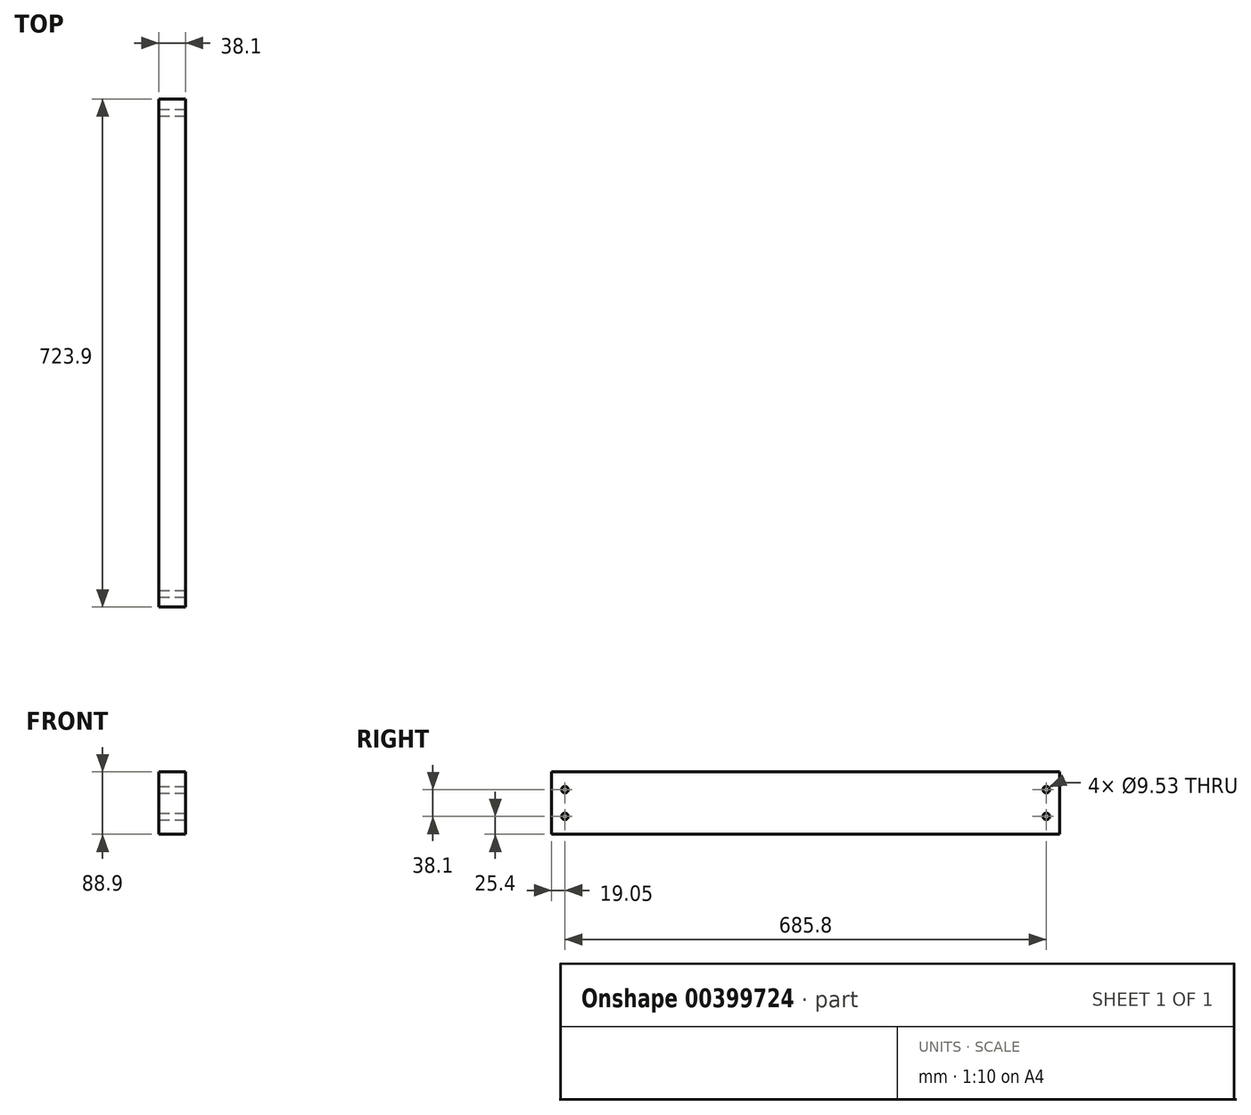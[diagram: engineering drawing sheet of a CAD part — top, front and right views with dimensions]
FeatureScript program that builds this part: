
annotation { "Feature Type Name" : "Feature", "Feature Type Description" : "" }
export const myFeature = defineFeature(function(context is Context, id is Id, definition is map)
    precondition{}
    {
        {
            var Q0;
            Q0=qCreatedBy(makeId("Front.planeOp"),FACE);
            var sketch = newSketch(context, id + "F0", { "sketchPlane" : qUnion([Q0])});
            skLineSegment(sketch, "E0.bottom", {"start": v(-19.05, 44.45) * mm, "end": v(19.05, 44.45) * mm});
            skLineSegment(sketch, "E0.top", {"start": v(-19.05, -44.45) * mm, "end": v(19.05, -44.45) * mm});
            skLineSegment(sketch, "E0.left", {"start": v(-19.05, 44.45) * mm, "end": v(-19.05, -44.45) * mm});
            skLineSegment(sketch, "E0.right", {"start": v(19.05, 44.45) * mm, "end": v(19.05, -44.45) * mm});
            skSolve(sketch);
        }
        {
            var Q0;
            Q0 = qSketchRegion(id + "F0", true);
            extrude(context, id + "F1", {"entities" : qUnion([Q0]), "endBound" : BoundingType.SYMMETRIC, "depth" : 723.9 * mm});
        }
        {
            var Q0;
            Q0=makeQuery(id+"F1.opExtrude","SWEPT_FACE",FACE,{"disambiguationData":[OSD([sQuery(id+"F0.wireOp",EDGE,"E0.right")])]});
            var sketch = newSketch(context, id + "F2", { "sketchPlane" : qUnion([Q0])});
            skCircle(sketch, "E1", {"center": v(-342.9, 19.05) * mm, "radius": 4.76 * mm});
            skCircle(sketch, "E2", {"center": v(-342.9, -19.05) * mm, "radius": 4.76 * mm});
            skCircle(sketch, "E3", {"center": v(342.9, 19.05) * mm, "radius": 4.76 * mm});
            skCircle(sketch, "E4", {"center": v(342.9, -19.05) * mm, "radius": 4.76 * mm});
            skSolve(sketch);
        }
        {
            var Q0;
            Q0 = qSketchRegion(id + "F2", true);
            extrude(context, id + "F3", {"entities" : qUnion([Q0]), "operationType" : NewBodyOperationType.REMOVE, "endBound" : BoundingType.THROUGH_ALL, "oppositeDirection" : true, "depth" : 25.4 * mm});
        }
    });
